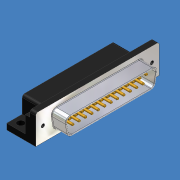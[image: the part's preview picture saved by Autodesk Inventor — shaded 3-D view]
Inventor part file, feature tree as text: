
AUTODESK INVENTOR PART (.ipt)
format: ipt  version: unknown  size: 348,672 bytes
history: native  units: mm (DEFAULTED — no unit token found)
features: sketch x6, extrude x4, fillet x3, hole x2, pattern_linear x1
ambient origin geometry x8: Origin, YZ Plane, XZ Plane, XY Plane, X Axis, Y Axis, Z Axis, Center Point
feature tree (16):
  extrude  "Extrusion1"  Depth=12.5mm
  extrude  "Extrusion4"  Depth=17.453293mm
  extrude  "Extrusion2"  Depth=38.38mm
  fillet  "Fillet1"  Radius=0.5mm
  hole  "Hole1"  [1 undecoded]
  extrude  "Extrusion3"  Depth=1.42mm
  fillet  "Fillet2"  Radius=16.55mm
  pattern_linear  "Rectangular Pattern1"  Spacing1=5.0mm  [1 undecoded]
  fillet  "Fillet3"  Radius=1.0mm
  hole  "Hole2"  [1 undecoded]
  sketch  "Sketch1"  dims[d4=12.5mm d5=12.5mm]
  sketch  "Sketch2"  dims[d6=53.2mm d7=0.0mm d9=17.453293mm]
  sketch  "Sketch3"  dims[d11=1.5mm d12=38.38mm d13=0.5mm]
  sketch  "Sketch4"  dims[d14=6.1mm d15=0.0mm d16=0.25mm]
  sketch  "Sketch6"  dims[d17=47.0mm]
  sketch  "Sketch7"  dims[d18=1.5mm d19=6.0mm d20=4.0mm d21=2.0mm d22=14.3117mm d23=8.0mm d24=20.594885mm d27=1.42mm d28=16.55mm d29=5.0mm d30=0.0mm d31=1.0mm d32=0.5mm d33=250.0mm d35=1.379mm d36=20.0mm d38=2.84mm d40=2.75mm d41=2.5mm d42=39.75mm d43=2.0mm d44=7.25mm d45=0.0mm d46=1.0mm d47=9.525mm d48=47.0mm d49=3.0mm d50=6.0mm d51=4.0mm d52=2.0mm d53=14.3117mm d54=8.0mm d55=20.594885mm d56=7.9mm]
note: 3 required parameter values undecoded (feature->parameter linkage not recoverable at this tier; creation-order binding heuristic only, values carry confidence <= 0.55)
